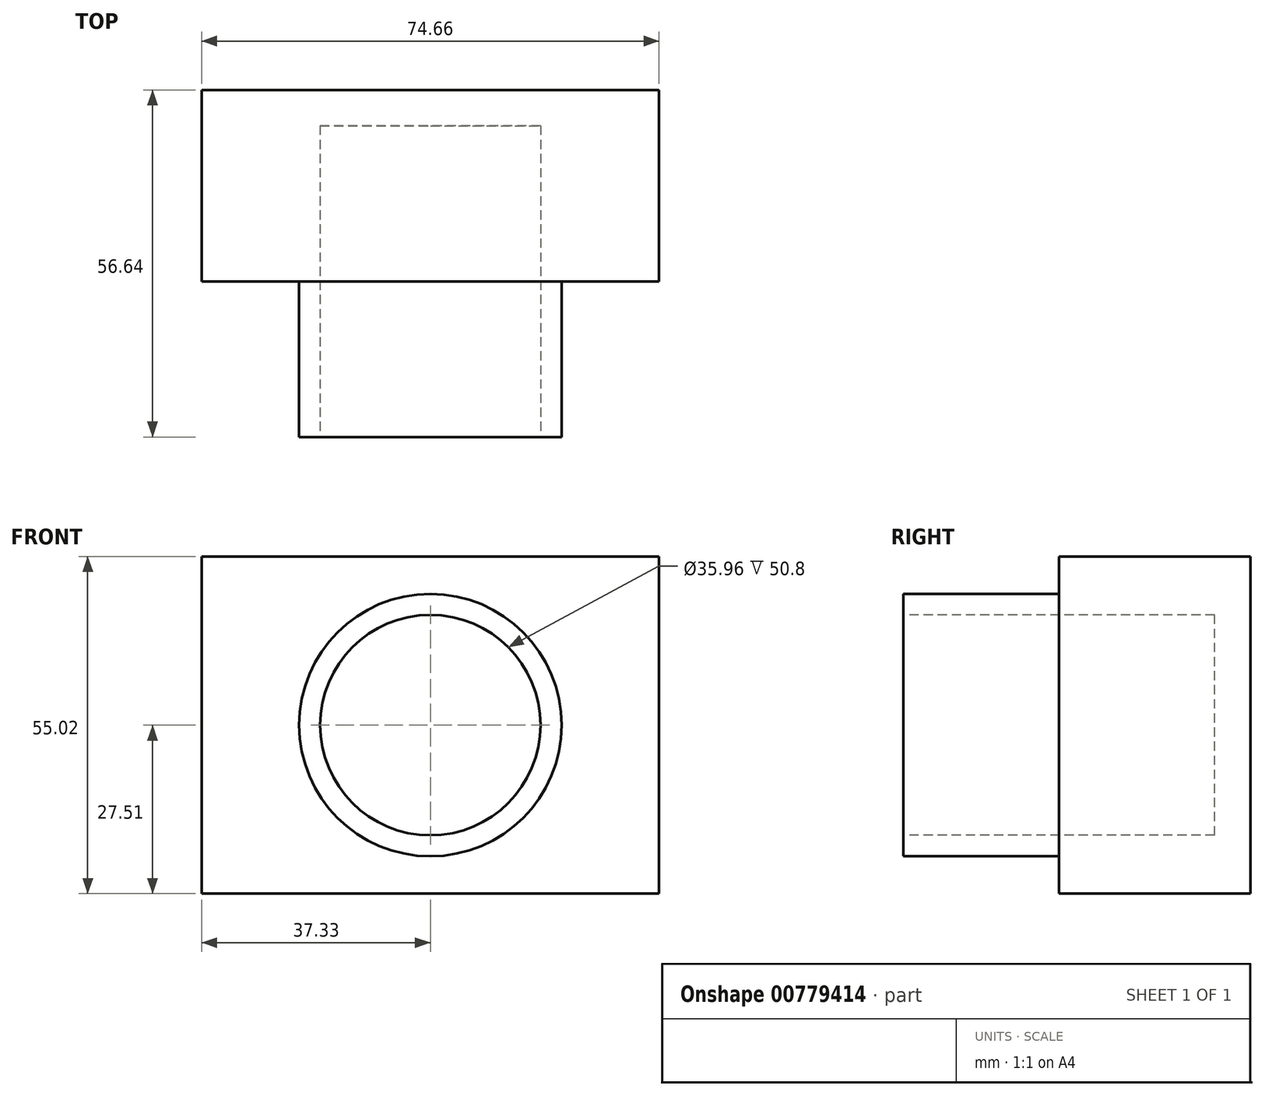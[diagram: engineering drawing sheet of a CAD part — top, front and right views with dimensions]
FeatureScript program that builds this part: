
annotation { "Feature Type Name" : "Feature", "Feature Type Description" : "" }
export const myFeature = defineFeature(function(context is Context, id is Id, definition is map)
    precondition{}
    {
        {
            var Q0;
            Q0=qCreatedBy(makeId("Front.planeOp"),FACE);
            var sketch = newSketch(context, id + "F0", { "sketchPlane" : qUnion([Q0])});
            skLineSegment(sketch, "E0.bottom", {"start": v(37.33, 27.51) * mm, "end": v(-37.33, 27.51) * mm});
            skLineSegment(sketch, "E0.top", {"start": v(37.33, -27.51) * mm, "end": v(-37.33, -27.51) * mm});
            skLineSegment(sketch, "E0.left", {"start": v(37.33, 27.51) * mm, "end": v(37.33, -27.51) * mm});
            skLineSegment(sketch, "E0.right", {"start": v(-37.33, 27.51) * mm, "end": v(-37.33, -27.51) * mm});
            skPoint(sketch, "E0.middle", {"position": v(0, 0) * mm});
            skSolve(sketch);
        }
        {
            var Q0;
            Q0=makeQuery(id+"F0.imprint","IMPRINT",FACE,{"disambiguationData":[TD([[makeQuery(id+"F0.imprint","IMPRINT",EDGE,{"derivedFrom":sQuery(id+"F0.wireOp",EDGE,"E0.bottom")}),1.0]])]});
            extrude(context, id + "F1", {"entities" : qUnion([Q0]), "depth" : 31.24 * mm, "offsetDistance" : 25.4 * mm});
        }
        {
            var Q0;
            Q0=makeQuery(id+"F1.opExtrude","CAP_FACE",FACE,{"disambiguationData":[OSD([sQuery(id+"F0.wireOp",EDGE,"E0.bottom"),sQuery(id+"F0.wireOp",EDGE,"E0.top"),sQuery(id+"F0.wireOp",EDGE,"E0.left"),sQuery(id+"F0.wireOp",EDGE,"E0.right")])],"isStart":false});
            var sketch = newSketch(context, id + "F2", { "sketchPlane" : qUnion([Q0])});
            skCircle(sketch, "E1", {"center": v(0, 0) * mm, "radius": 21.4 * mm});
            skSolve(sketch);
        }
        {
            var Q0;
            Q0=makeQuery(id+"F2.imprint","IMPRINT",FACE,{"disambiguationData":[TD([[makeQuery(id+"F2.imprint","IMPRINT",EDGE,{"derivedFrom":sQuery(id+"F2.wireOp",EDGE,"E1")}),1.0]])]});
            extrude(context, id + "F3", {"entities" : qUnion([Q0]), "operationType" : NewBodyOperationType.ADD, "depth" : 25.4 * mm, "offsetDistance" : 25.4 * mm});
        }
        {
            var Q0;
            Q0=makeQuery(id+"F3.opExtrude","CAP_FACE",FACE,{"disambiguationData":[OSD([sQuery(id+"F2.wireOp",EDGE,"E1")])],"isStart":false});
            var sketch = newSketch(context, id + "F4", { "sketchPlane" : qUnion([Q0])});
            skCircle(sketch, "E2", {"center": v(0, 0) * mm, "radius": 17.98 * mm});
            skSolve(sketch);
        }
        {
            var Q0;
            Q0=makeQuery(id+"F4.imprint","IMPRINT",FACE,{"disambiguationData":[TD([[makeQuery(id+"F4.imprint","IMPRINT",EDGE,{"derivedFrom":sQuery(id+"F4.wireOp",EDGE,"E2")}),1.0]])]});
            extrude(context, id + "F5", {"entities" : qUnion([Q0]), "operationType" : NewBodyOperationType.REMOVE, "oppositeDirection" : true, "depth" : 25.4 * mm, "offsetDistance" : 25.4 * mm});
        }
        {
            var Q0;
            Q0=makeQuery(id+"F5.boolean.opBoolean","COPY",FACE,{"derivedFrom":makeQuery(id+"F5.opExtrude","CAP_FACE",FACE,{"disambiguationData":[OSD([sQuery(id+"F4.wireOp",EDGE,"E2")])],"isStart":false})});
            extrude(context, id + "F6", {"entities" : qUnion([Q0]), "operationType" : NewBodyOperationType.REMOVE, "oppositeDirection" : true, "depth" : 25.4 * mm, "offsetDistance" : 25.4 * mm});
        }
    });
